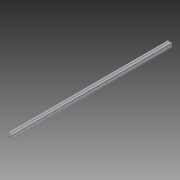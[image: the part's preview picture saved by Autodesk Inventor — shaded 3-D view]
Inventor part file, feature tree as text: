
AUTODESK INVENTOR PART (.ipt)
format: ipt  version: 2013 (Build 170138000, 138)  size: 285,696 bytes
history: native  units: in
note: dims shown in document units (in); Inventor stores cm internally (conversion verified against a paired STEP export)
features: extrude x1, sketch x1
ambient origin geometry x8: Origin, YZ Plane, XZ Plane, XY Plane, X Axis, Y Axis, Z Axis, Center Point
bodies: Solid1 (feature_tree)
feature tree (2):
  extrude  "Extrusion1"  [1 undecoded]
  sketch  "Sketch1"  dims[d0=56.0in d1=0.0in]
note: 1 required parameter value undecoded (feature->parameter linkage not recoverable at this tier; creation-order binding heuristic only, values carry confidence <= 0.55)
